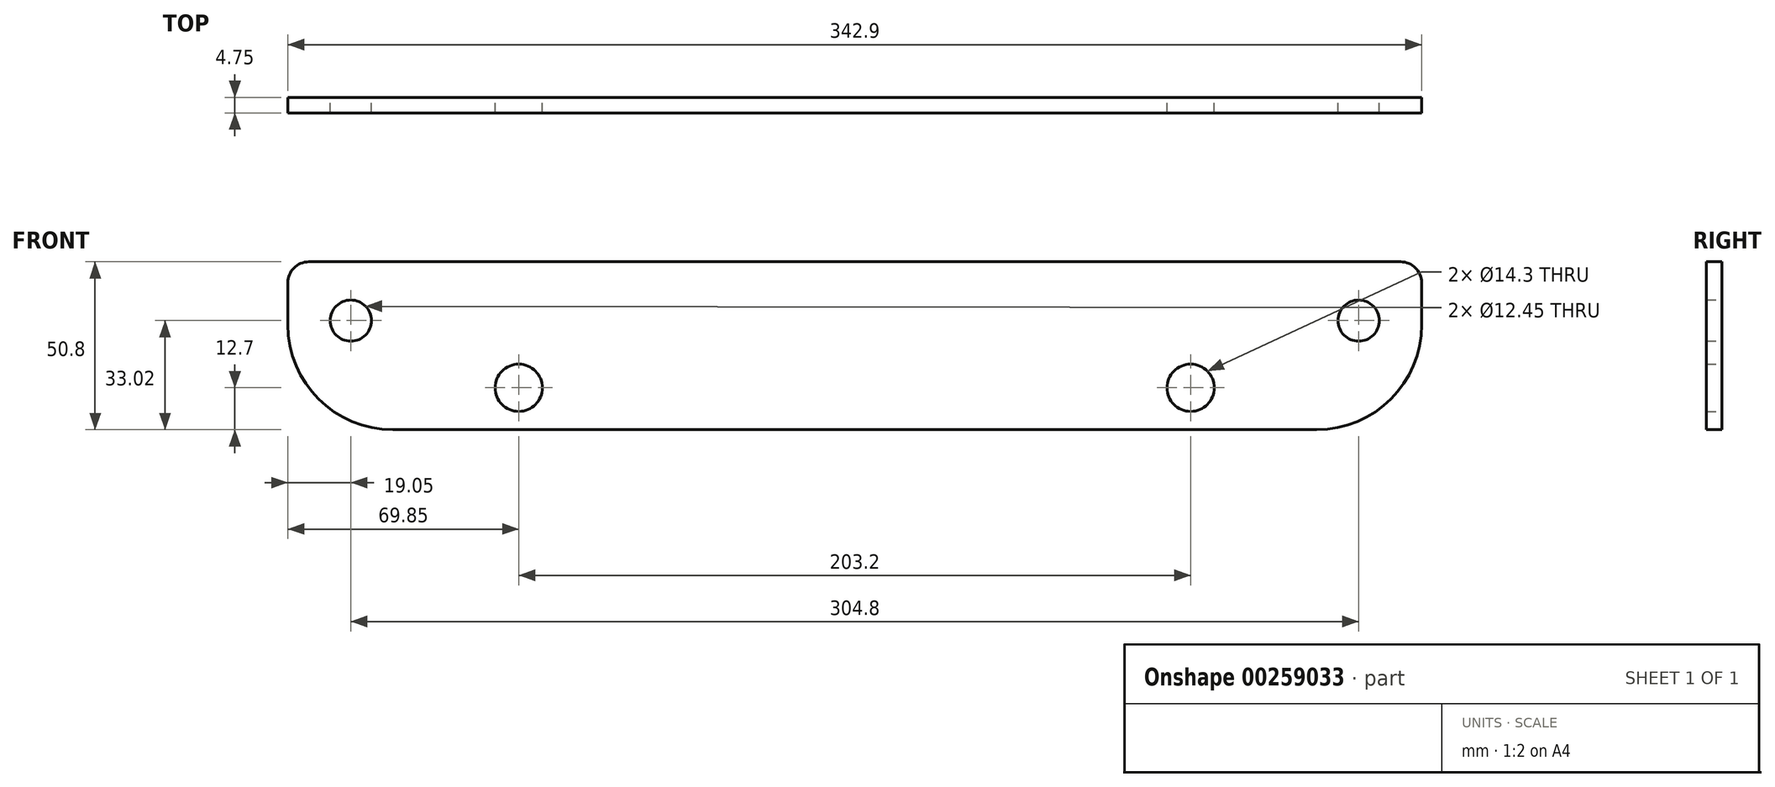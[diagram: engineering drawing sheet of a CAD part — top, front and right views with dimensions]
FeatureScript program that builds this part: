
annotation { "Feature Type Name" : "Feature", "Feature Type Description" : "" }
export const myFeature = defineFeature(function(context is Context, id is Id, definition is map)
    precondition{}
    {
        {
            var Q0;
            Q0=qCreatedBy(makeId("Front.planeOp"),FACE);
            var sketch = newSketch(context, id + "F0", { "sketchPlane" : qUnion([Q0])});
            skLineSegment(sketch, "E0.bottom", {"start": v(139.7, -25.4) * mm, "end": v(-139.7, -25.4) * mm});
            skLineSegment(sketch, "E0.top", {"start": v(165.1, 25.4) * mm, "end": v(-165.1, 25.4) * mm});
            skLineSegment(sketch, "E0.left", {"start": v(171.45, 6.35) * mm, "end": v(171.45, 19.05) * mm});
            skLineSegment(sketch, "E0.right", {"start": v(-171.45, 6.35) * mm, "end": v(-171.45, 19.05) * mm});
            skPoint(sketch, "E0.middle", {"position": v(0, 0) * mm});
            skCircle(sketch, "E1", {"center": v(-101.6, -12.7) * mm, "radius": 7.15 * mm});
            skPoint(sketch, "E2.visualSharp", {"position": v(-171.45, 25.4) * mm});
            skArc(sketch, "E2.filletArc", {"start": v(-165.1, 25.4) * mm, "mid": v(-169.6, 23.54) * mm, "end": v(-171.45, 19.05) * mm});
            skPoint(sketch, "E3.visualSharp", {"position": v(171.45, 25.4) * mm});
            skArc(sketch, "E3.filletArc", {"start": v(171.45, 19.05) * mm, "mid": v(169.6, 23.54) * mm, "end": v(165.1, 25.4) * mm});
            skCircle(sketch, "E4.MirrorC", {"center": v(101.6, -12.7) * mm, "radius": 7.15 * mm});
            skCircle(sketch, "E5", {"center": v(-152.4, 7.62) * mm, "radius": 6.23 * mm});
            skLineSegment(sketch, "E6", {"start": v(0, -25.4) * mm, "end": v(0, -25.4) * mm});
            skArc(sketch, "E7.filletArc", {"start": v(-171.45, 6.35) * mm, "mid": v(-162.15, -16.1) * mm, "end": v(-139.7, -25.4) * mm});
            skArc(sketch, "E8.MirrorCS", {"start": v(171.45, 6.35) * mm, "mid": v(162.15, -16.1) * mm, "end": v(139.7, -25.4) * mm});
            skCircle(sketch, "E9.MirrorC", {"center": v(152.4, 7.62) * mm, "radius": 6.23 * mm});
            skSolve(sketch);
        }
        {
            var Q0;
            Q0=makeQuery(id+"F0.imprint","IMPRINT",FACE,{"disambiguationData":[TD([[makeQuery(id+"F0.imprint","IMPRINT",EDGE,{"derivedFrom":sQuery(id+"F0.wireOp",EDGE,"E0.bottom")}),-1.0]])]});
            extrude(context, id + "F1", {"entities" : qUnion([Q0]), "depth" : 4.75 * mm});
        }
    });
